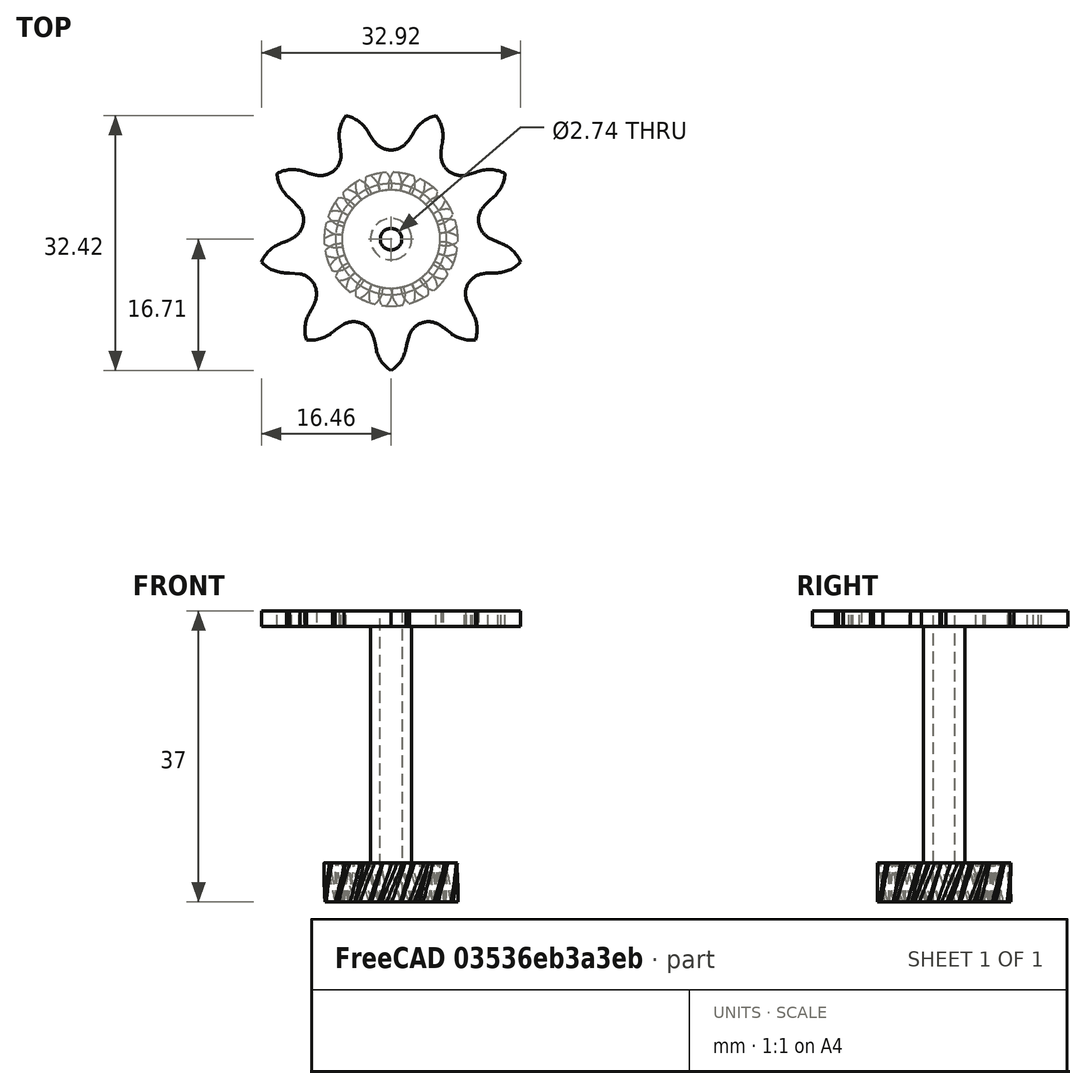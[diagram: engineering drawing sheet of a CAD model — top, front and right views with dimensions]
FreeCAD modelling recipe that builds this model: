
FCSTD DOCUMENT  (FreeCAD 0.21R33771 (Git))
Label: kosozubaja
License: All rights reserved
LicenseURL: https://en.wikipedia.org/wiki/All_rights_reserved
objects: Sketcher::SketchObject×2, PartDesign::Pad×2, PartDesign::FeaturePython×1, Part::Part2DObjectPython×1, PartDesign::Pocket×1, PartDesign::Body×1
note: 11 computed .brp shape members not serialized (recipe doc carries the construction recipe); baked Part::Feature solids carry a one-line shape summary decoded from their .brp

FEATURE [PartDesign::FeaturePython] InvoluteGear  # WARN: FeaturePython — macro-defined, semantics opaque (R4)
  AttacherType = Attacher::AttachEngine3D
  angular_backlash = 0
  backlash = 0
  beta = 20
  clearance = 0.25
  da = 17
  df = 12.5
  double_helix = false
  dw = 15
  head = 0
  head_fillet = 0
  height = 5
  module = 1
  numpoints = 20
  pressure_angle = 20
  properties_from_tool = false
  reversed_backlash = false
  root_fillet = 0
  shift = 0
  simple = false
  teeth = 15
  transverse_pitch = 3.14159
  traverse_module = 1
  undercut = false
  version = 1.2.0
  expr: angular_backlash = backlash / dw * 360 ° / pi
FEATURE [Sketcher::SketchObject] Sketch
  FullyConstrained = false
  MapMode = 5
  Placement = pos=(0.000451196,0.000111728,5.00093) rot=(-0.240366,0.970682,-1.1e-05;9.3e-05rad)
  Support = -> [InvoluteGear]
  sketch-geometry (1):
    g0: Circle CenterX=0 CenterY=0 CenterZ=0 NormalX=0 NormalY=0 NormalZ=1 AngleXU=0 Radius=2.62188
  constraints (1):
    c: Coincident(g0,g-1)
FEATURE [PartDesign::Pad] Pad
  BaseFeature = -> InvoluteGear
  Direction = (9.02224e-05,2.23414e-05,1)
  Length = 30
  Length2 = 10
  Profile = -> Sketch
  ReferenceAxis = -> Sketch [N_Axis]
  Type = 0
FEATURE [Part::Part2DObjectPython] Sprocket  # Draft 2D object (typed FeaturePython)
  NumberOfTeeth = 9
  Pitch = 9.52
  Placement = pos=(0,0,35) rot=(0,0,1;0rad)
  RollerDiameter = 5.08
  SprocketReference = 1
  Thickness = 4.27
FEATURE [PartDesign::Pad] Pad001
  BaseFeature = -> Pad
  Direction = (0,0,1)
  Length = 2
  Length2 = 10
  Profile = -> Sprocket
  ReferenceAxis = -> Sprocket [N_Axis]
  Type = 0
FEATURE [Sketcher::SketchObject] Sketch001
  FullyConstrained = false
  MapMode = 5
  Placement = pos=(0,0,37) rot=(0,0,1;0rad)
  Support = -> [Pad001]
  sketch-geometry (1):
    g0: Circle CenterX=0 CenterY=0 CenterZ=0 NormalX=0 NormalY=0 NormalZ=1 AngleXU=0 Radius=1.37027
  constraints (1):
    c: Coincident(g0,g-1)
FEATURE [PartDesign::Pocket] Pocket
  BaseFeature = -> Pad001
  Direction = (0,0,-1)
  Length = 5
  Length2 = 5
  Profile = -> Sketch001
  ReferenceAxis = -> Sketch001 [N_Axis]
  Type = 1
FEATURE [PartDesign::Body] Body
  Group = -> [InvoluteGear,Sketch,Pad,Sprocket,Pad001,Sketch001,Pocket]
  Origin = -> Origin
  Tip = -> Pocket
